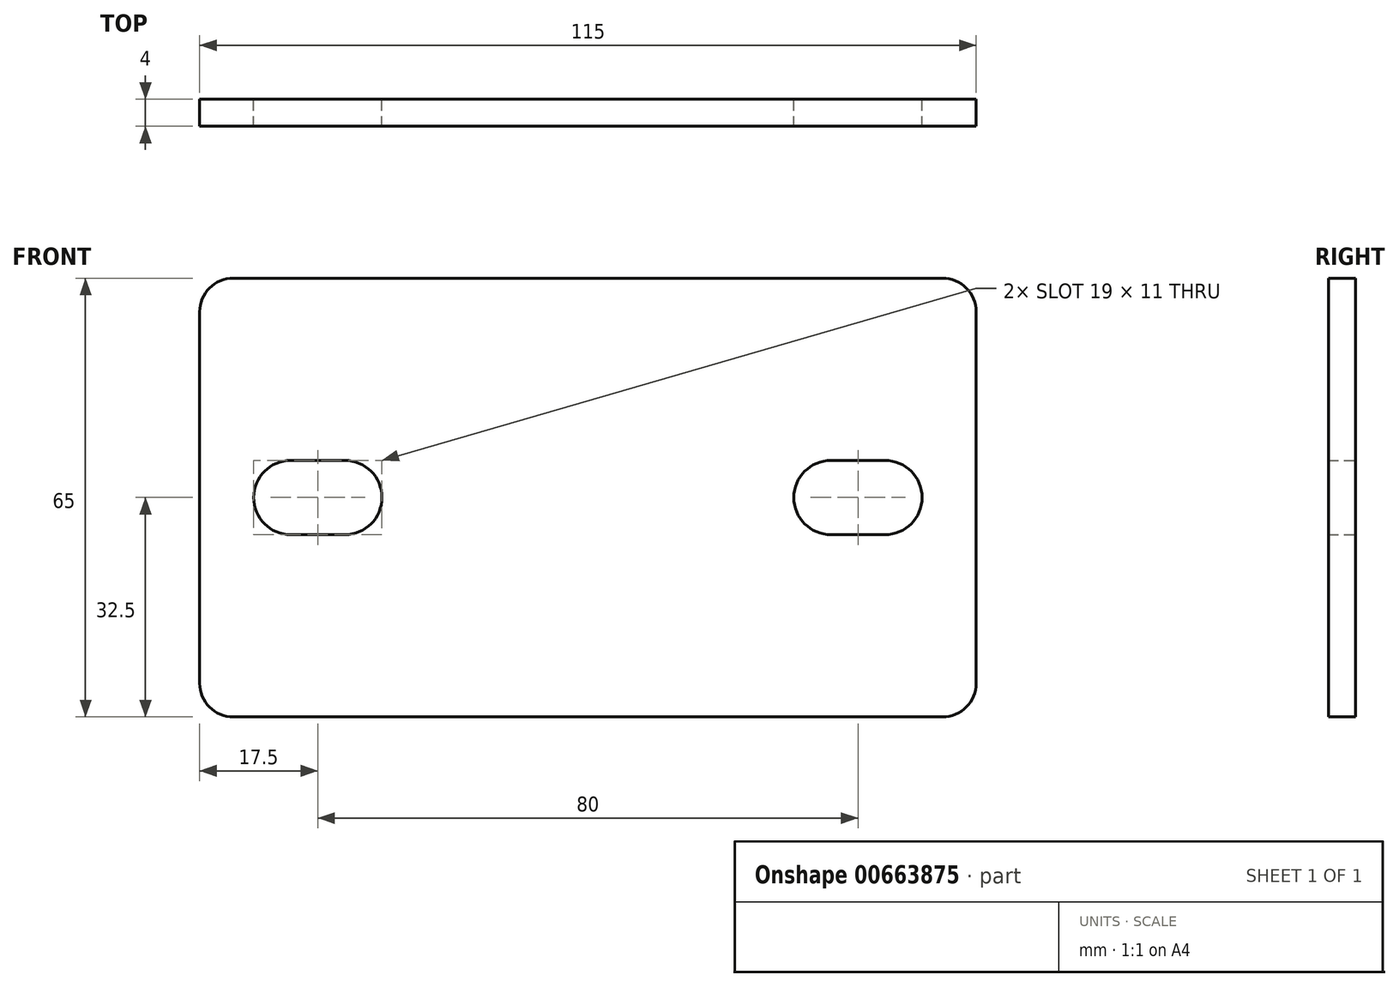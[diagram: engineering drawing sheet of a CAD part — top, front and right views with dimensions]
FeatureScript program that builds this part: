
annotation { "Feature Type Name" : "Feature", "Feature Type Description" : "" }
export const myFeature = defineFeature(function(context is Context, id is Id, definition is map)
    precondition{}
    {
        {
            var Q0;
            Q0=qCreatedBy(makeId("Front.planeOp"),FACE);
            var sketch = newSketch(context, id + "F0", { "sketchPlane" : qUnion([Q0])});
            skLineSegment(sketch, "E0.bottom", {"start": v(57.5, 32.5) * mm, "end": v(-57.5, 32.5) * mm});
            skLineSegment(sketch, "E0.top", {"start": v(57.5, -32.5) * mm, "end": v(-57.5, -32.5) * mm});
            skLineSegment(sketch, "E0.left", {"start": v(57.5, 32.5) * mm, "end": v(57.5, -32.5) * mm});
            skLineSegment(sketch, "E0.right", {"start": v(-57.5, 32.5) * mm, "end": v(-57.5, -32.5) * mm});
            skPoint(sketch, "E0.middle", {"position": v(0, 0) * mm});
            skLineSegment(sketch, "E1.bottom", {"start": v(-36, -5.5) * mm, "end": v(-44, -5.5) * mm});
            skLineSegment(sketch, "E1.top", {"start": v(-36, 5.5) * mm, "end": v(-44, 5.5) * mm});
            skLineSegment(sketch, "E1.left", {"start": v(-36, -5.5) * mm, "end": v(-36, 5.5) * mm, "construction": true});
            skLineSegment(sketch, "E1.right", {"start": v(-44, -5.5) * mm, "end": v(-44, 5.5) * mm, "construction": true});
            skPoint(sketch, "E1.middle", {"position": v(-40, 0) * mm});
            skArc(sketch, "E2", {"start": v(-44, 5.5) * mm, "mid": v(-49.5, 0) * mm, "end": v(-44, -5.5) * mm});
            skArc(sketch, "E3", {"start": v(-36, -5.5) * mm, "mid": v(-30.5, 0) * mm, "end": v(-36, 5.5) * mm});
            skArc(sketch, "E4.MirrorCS", {"start": v(36, -5.5) * mm, "mid": v(30.5, 0) * mm, "end": v(36, 5.5) * mm});
            skArc(sketch, "E5.MirrorCS", {"start": v(44, 5.5) * mm, "mid": v(49.5, 0) * mm, "end": v(44, -5.5) * mm});
            skLineSegment(sketch, "E6.MirrorCS", {"start": v(36, -5.5) * mm, "end": v(36, 5.5) * mm, "construction": true});
            skLineSegment(sketch, "E7.MirrorCS", {"start": v(44, -5.5) * mm, "end": v(44, 5.5) * mm, "construction": true});
            skLineSegment(sketch, "E8.MirrorCS", {"start": v(36, 5.5) * mm, "end": v(44, 5.5) * mm});
            skPoint(sketch, "E9.MirrorP", {"position": v(40, 0) * mm});
            skLineSegment(sketch, "E10.MirrorCS", {"start": v(36, -5.5) * mm, "end": v(44, -5.5) * mm});
            skSolve(sketch);
        }
        {
            var Q0;
            Q0=makeQuery(id+"F0.imprint","IMPRINT",FACE,{"disambiguationData":[TD([[makeQuery(id+"F0.imprint","IMPRINT",EDGE,{"derivedFrom":sQuery(id+"F0.wireOp",EDGE,"E0.bottom")}),1.0]])]});
            extrude(context, id + "F1", {"entities" : qUnion([Q0]), "depth" : 4 * mm, "offsetDistance" : 25 * mm});
        }
        {
            var Q0;
            Q0=makeQuery(id+"F1.opExtrude","SWEPT_EDGE",EDGE,{"disambiguationData":[OSD([sQuery(id+"F0.wireOp",EDGE,"E0.top"),sQuery(id+"F0.wireOp",EDGE,"E0.right")])]});
            var Q1;
            Q1=makeQuery(id+"F1.opExtrude","SWEPT_EDGE",EDGE,{"disambiguationData":[OSD([sQuery(id+"F0.wireOp",EDGE,"E0.bottom"),sQuery(id+"F0.wireOp",EDGE,"E0.right")])]});
            var Q2;
            Q2=makeQuery(id+"F1.opExtrude","SWEPT_EDGE",EDGE,{"disambiguationData":[OSD([sQuery(id+"F0.wireOp",EDGE,"E0.top"),sQuery(id+"F0.wireOp",EDGE,"E0.left")])]});
            var Q3;
            Q3=makeQuery(id+"F1.opExtrude","SWEPT_EDGE",EDGE,{"disambiguationData":[OSD([sQuery(id+"F0.wireOp",EDGE,"E0.bottom"),sQuery(id+"F0.wireOp",EDGE,"E0.left")])]});
            fillet(context, id + "F2", {"entities" : qUnion([Q0, Q1, Q2, Q3]), "radius" : 5 * mm, "tangentPropagation" : true, "allowEdgeOverflow" : false});
        }
    });
